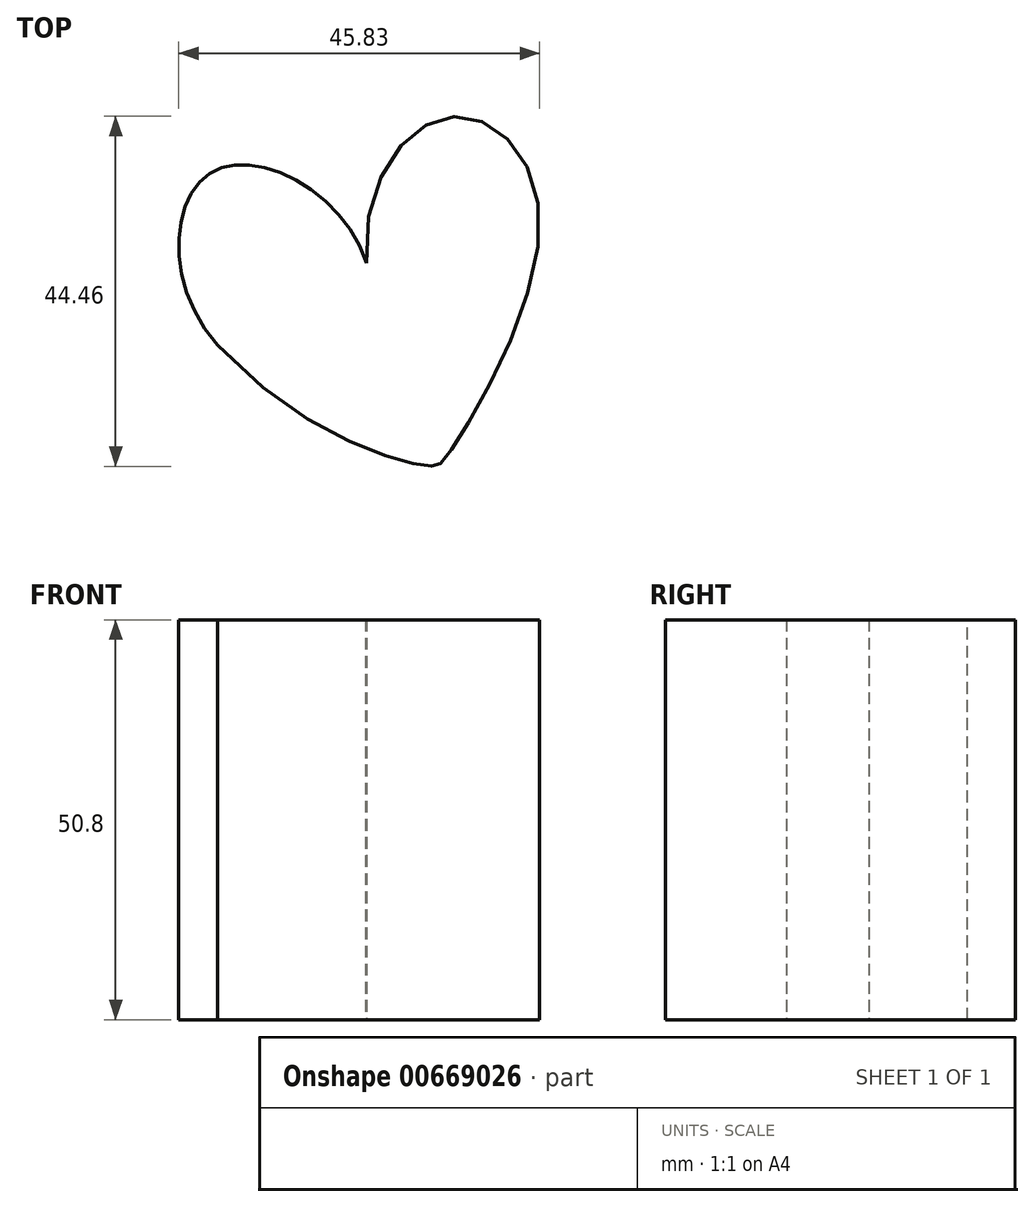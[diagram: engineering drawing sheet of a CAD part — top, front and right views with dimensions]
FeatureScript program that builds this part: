
annotation { "Feature Type Name" : "Feature", "Feature Type Description" : "" }
export const myFeature = defineFeature(function(context is Context, id is Id, definition is map)
    precondition{}
    {
        {
            var Q0;
            Q0=qCreatedBy(makeId("Top.planeOp"),FACE);
            var sketch = newSketch(context, id + "F0", { "sketchPlane" : qUnion([Q0])});
            skFitSpline(sketch, "E0", {"points": [v(-65.46, 7.27) * mm, v(-38.32, -8.1) * mm, v(-36.6, -7.15) * mm, v(-24.57, 23.16) * mm, v(-35.47, 36.34) * mm, v(-46.55, 17.74) * mm], "startDerivative": vector(131.91, -139.9) * mm, "endDerivative": vector(11.68, -142.78) * mm});
            skFitSpline(sketch, "E1", {"points": [v(-65.46, 7.27) * mm, v(-65.83, 29.48) * mm, v(-46.55, 17.74) * mm], "startDerivative": vector(-41.73, 47.3) * mm, "endDerivative": vector(16.45, -52.5) * mm});
            skSolve(sketch);
        }
        {
            var Q0;
            Q0=makeQuery(id+"F0.imprint","IMPRINT",FACE,{"disambiguationData":[TD([[makeQuery(id+"F0.imprint","IMPRINT",EDGE,{"derivedFrom":sQuery(id+"F0.wireOp",EDGE,"E0")}),1.0]])]});
            extrude(context, id + "F1", {"entities" : qUnion([Q0]), "endBound" : BoundingType.SYMMETRIC, "depth" : 50.8 * mm, "offsetDistance" : 25.4 * mm});
        }
    });
